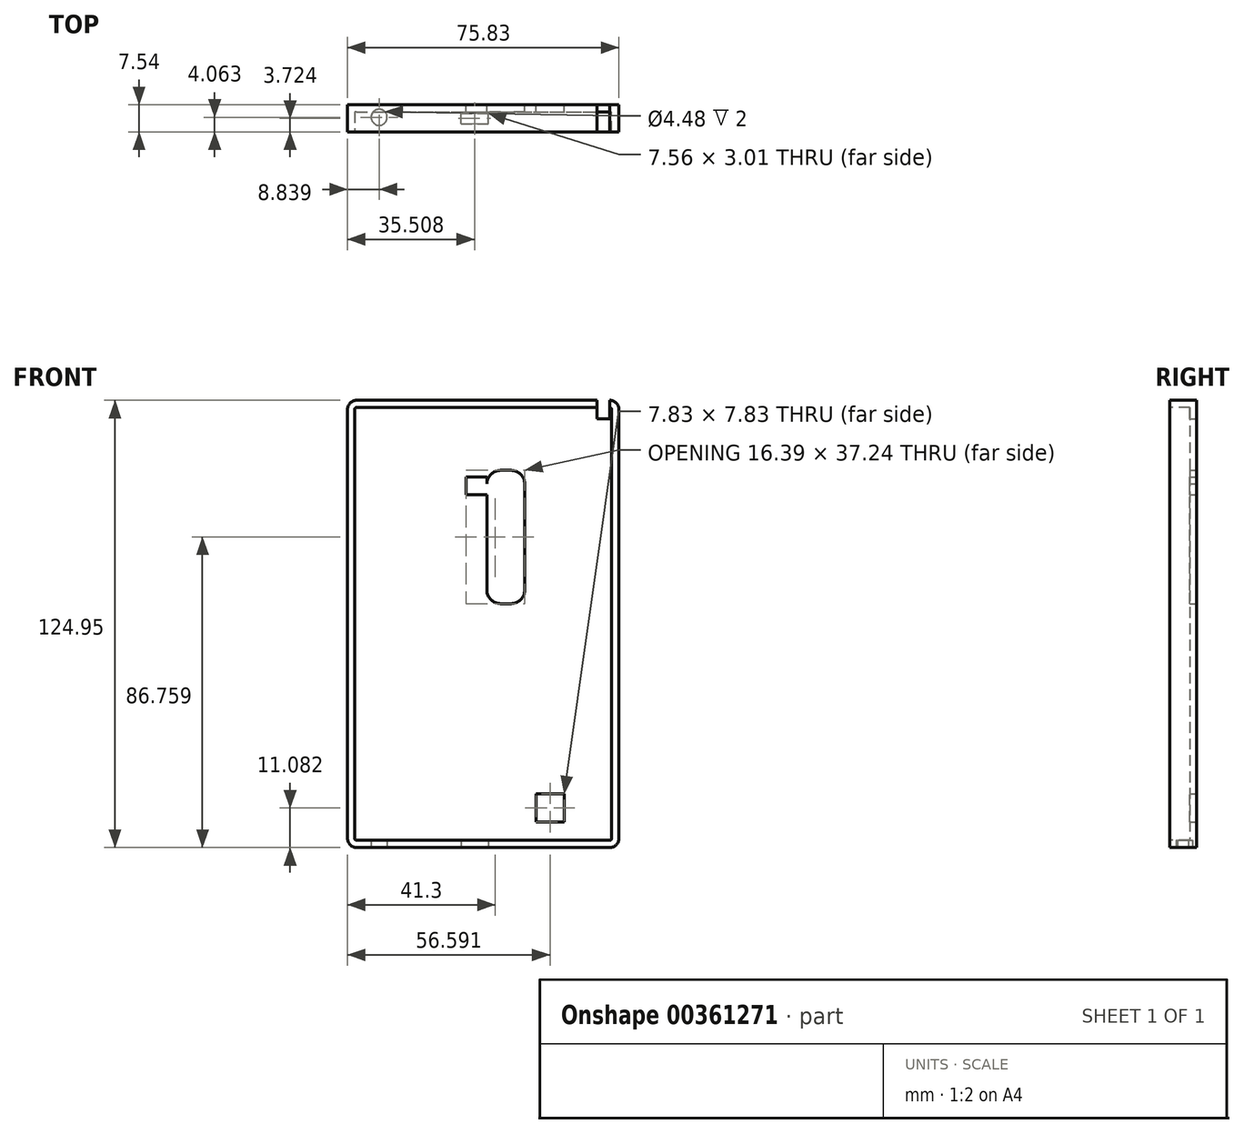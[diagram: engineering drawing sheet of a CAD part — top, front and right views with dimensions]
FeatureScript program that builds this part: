
annotation { "Feature Type Name" : "Feature", "Feature Type Description" : "" }
export const myFeature = defineFeature(function(context is Context, id is Id, definition is map)
    precondition{}
    {
        {
            var Q0;
            Q0=qCreatedBy(makeId("Front.planeOp"),FACE);
            var sketch = newSketch(context, id + "F0", { "sketchPlane" : qUnion([Q0])});
            skLineSegment(sketch, "E0.bottom", {"start": v(-33.05, 55.46) * mm, "end": v(37.7, 55.46) * mm});
            skLineSegment(sketch, "E0.top", {"start": v(-33.05, -69.49) * mm, "end": v(37.7, -69.49) * mm});
            skLineSegment(sketch, "E0.left", {"start": v(-35.6, 52.92) * mm, "end": v(-35.6, -66.95) * mm});
            skLineSegment(sketch, "E0.right", {"start": v(40.24, 52.92) * mm, "end": v(40.24, -66.95) * mm});
            skPoint(sketch, "E1.visualSharp", {"position": v(-35.6, 55.46) * mm});
            skArc(sketch, "E1.filletArc", {"start": v(-33.05, 55.46) * mm, "mid": v(-34.85, 54.72) * mm, "end": v(-35.6, 52.92) * mm});
            skPoint(sketch, "E2.visualSharp", {"position": v(40.24, 55.46) * mm});
            skArc(sketch, "E2.filletArc", {"start": v(40.24, 52.92) * mm, "mid": v(39.5, 54.72) * mm, "end": v(37.7, 55.46) * mm});
            skPoint(sketch, "E3.visualSharp", {"position": v(40.24, -69.49) * mm});
            skArc(sketch, "E3.filletArc", {"start": v(37.7, -69.49) * mm, "mid": v(39.5, -68.74) * mm, "end": v(40.24, -66.95) * mm});
            skPoint(sketch, "E4.visualSharp", {"position": v(-35.6, -69.49) * mm});
            skArc(sketch, "E4.filletArc", {"start": v(-35.6, -66.95) * mm, "mid": v(-34.85, -68.74) * mm, "end": v(-33.05, -69.49) * mm});
            skSolve(sketch);
        }
        {
            var Q0;
            Q0=makeQuery(id+"F0.imprint","IMPRINT",FACE,{"disambiguationData":[TD([[makeQuery(id+"F0.imprint","IMPRINT",EDGE,{"derivedFrom":sQuery(id+"F0.wireOp",EDGE,"E0.bottom")}),-1.0]])]});
            extrude(context, id + "F1", {"entities" : qUnion([Q0]), "oppositeDirection" : true, "depth" : 7.54 * mm});
        }
        {
            var Q0;
            Q0=makeQuery(id+"F1.opExtrude","SWEPT_FACE",FACE,{"disambiguationData":[OSD([sQuery(id+"F0.wireOp",EDGE,"E0.top")])]});
            var sketch = newSketch(context, id + "F2", { "sketchPlane" : qUnion([Q0])});
            skLineSegment(sketch, "E5.bottom", {"start": v(-3.86, -2.22) * mm, "end": v(3.7, -2.22) * mm});
            skLineSegment(sketch, "E5.top", {"start": v(-3.86, -5.23) * mm, "end": v(3.7, -5.23) * mm});
            skLineSegment(sketch, "E5.left", {"start": v(-3.86, -2.22) * mm, "end": v(-3.86, -5.23) * mm});
            skLineSegment(sketch, "E5.right", {"start": v(3.7, -2.22) * mm, "end": v(3.7, -5.23) * mm});
            skCircle(sketch, "E6", {"center": v(-26.75, -4.06) * mm, "radius": 2.24 * mm});
            skSolve(sketch);
        }
        {
            var Q0;
            Q0=makeQuery(id+"F1.opExtrude","CAP_FACE",FACE,{"disambiguationData":[OSD([sQuery(id+"F0.wireOp",EDGE,"E0.bottom"),sQuery(id+"F0.wireOp",EDGE,"E0.top"),sQuery(id+"F0.wireOp",EDGE,"E0.left"),sQuery(id+"F0.wireOp",EDGE,"E0.right"),sQuery(id+"F0.wireOp",EDGE,"E1.filletArc"),sQuery(id+"F0.wireOp",EDGE,"E2.filletArc"),sQuery(id+"F0.wireOp",EDGE,"E3.filletArc"),sQuery(id+"F0.wireOp",EDGE,"E4.filletArc")])],"isStart":false});
            var sketch = newSketch(context, id + "F3", { "sketchPlane" : qUnion([Q0])});
            skLineSegment(sketch, "E7.bottom", {"start": v(-10.1, 35.89) * mm, "end": v(-7.16, 35.89) * mm});
            skLineSegment(sketch, "E7.top", {"start": v(-10.1, -1.35) * mm, "end": v(-7.16, -1.35) * mm});
            skLineSegment(sketch, "E7.left", {"start": v(-13.9, 32.08) * mm, "end": v(-13.9, 2.46) * mm});
            skLineSegment(sketch, "E7.right", {"start": v(-3.35, 32.08) * mm, "end": v(-3.35, 2.46) * mm});
            skLineSegment(sketch, "E8.bottom", {"start": v(-13.9, 22.25) * mm, "end": v(-3.35, 22.25) * mm});
            skLineSegment(sketch, "E8.left", {"start": v(-13.9, 22.25) * mm, "end": v(-13.9, 2.46) * mm});
            skLineSegment(sketch, "E8.right", {"start": v(-3.35, 22.25) * mm, "end": v(-3.35, 2.46) * mm});
            skLineSegment(sketch, "E9.bottom", {"start": v(-12.5, 14.13) * mm, "end": v(-4.76, 14.13) * mm});
            skLineSegment(sketch, "E9.top", {"start": v(-12.5, 6.77) * mm, "end": v(-4.76, 6.77) * mm});
            skLineSegment(sketch, "E9.left", {"start": v(-12.5, 14.13) * mm, "end": v(-12.5, 6.77) * mm});
            skLineSegment(sketch, "E9.right", {"start": v(-4.76, 14.13) * mm, "end": v(-4.76, 6.77) * mm});
            skLineSegment(sketch, "E10.bottom", {"start": v(-3.35, 34.03) * mm, "end": v(2.49, 34.03) * mm});
            skLineSegment(sketch, "E10.top", {"start": v(-3.35, 29.07) * mm, "end": v(2.49, 29.07) * mm});
            skLineSegment(sketch, "E10.left", {"start": v(-3.35, 34.03) * mm, "end": v(-3.35, 29.07) * mm});
            skLineSegment(sketch, "E10.right", {"start": v(2.49, 34.03) * mm, "end": v(2.49, 29.07) * mm});
            skLineSegment(sketch, "E11.bottom", {"start": v(-37.7, 55.46) * mm, "end": v(-34.08, 55.46) * mm});
            skLineSegment(sketch, "E11.top", {"start": v(-37.7, 50.33) * mm, "end": v(-34.08, 50.33) * mm});
            skLineSegment(sketch, "E11.left", {"start": v(-37.7, 55.46) * mm, "end": v(-37.7, 50.33) * mm});
            skLineSegment(sketch, "E11.right", {"start": v(-34.08, 55.46) * mm, "end": v(-34.08, 50.33) * mm});
            skLineSegment(sketch, "E12.bottom", {"start": v(-24.92, -54.5) * mm, "end": v(-17.09, -54.5) * mm});
            skLineSegment(sketch, "E12.top", {"start": v(-24.92, -62.32) * mm, "end": v(-17.09, -62.32) * mm});
            skLineSegment(sketch, "E12.left", {"start": v(-24.92, -54.5) * mm, "end": v(-24.92, -62.32) * mm});
            skLineSegment(sketch, "E12.right", {"start": v(-17.09, -54.5) * mm, "end": v(-17.09, -62.32) * mm});
            skPoint(sketch, "E13.visualSharp", {"position": v(-13.9, 35.89) * mm});
            skArc(sketch, "E13.filletArc", {"start": v(-10.1, 35.89) * mm, "mid": v(-12.8, 34.77) * mm, "end": v(-13.9, 32.08) * mm});
            skPoint(sketch, "E14.visualSharp", {"position": v(-3.35, 35.89) * mm});
            skArc(sketch, "E14.filletArc", {"start": v(-3.35, 32.08) * mm, "mid": v(-4.47, 34.77) * mm, "end": v(-7.16, 35.89) * mm});
            skPoint(sketch, "E15.visualSharp", {"position": v(-13.9, -1.35) * mm});
            skArc(sketch, "E15.filletArc", {"start": v(-13.9, 2.46) * mm, "mid": v(-12.8, -0.24) * mm, "end": v(-10.1, -1.35) * mm});
            skPoint(sketch, "E16.visualSharp", {"position": v(-3.35, -1.35) * mm});
            skArc(sketch, "E16.filletArc", {"start": v(-7.16, -1.35) * mm, "mid": v(-4.47, -0.24) * mm, "end": v(-3.35, 2.46) * mm});
            skSolve(sketch);
        }
        {
            var Q0;
            Q0=makeQuery(id+"F1.opExtrude","CAP_FACE",FACE,{"disambiguationData":[OSD([sQuery(id+"F0.wireOp",EDGE,"E0.bottom"),sQuery(id+"F0.wireOp",EDGE,"E0.top"),sQuery(id+"F0.wireOp",EDGE,"E0.left"),sQuery(id+"F0.wireOp",EDGE,"E0.right"),sQuery(id+"F0.wireOp",EDGE,"E1.filletArc"),sQuery(id+"F0.wireOp",EDGE,"E2.filletArc"),sQuery(id+"F0.wireOp",EDGE,"E3.filletArc"),sQuery(id+"F0.wireOp",EDGE,"E4.filletArc")])],"isStart":true});
            shell(context, id + "F4", {"entities" : qUnion([Q0]), "thickness" : 2 * mm});
        }
        {
            var Q0;
            Q0 = qSketchRegion(id + "F3", true);
            extrude(context, id + "F5", {"entities" : qUnion([Q0]), "operationType" : NewBodyOperationType.REMOVE, "oppositeDirection" : true, "depth" : 50.8 * mm});
        }
        {
            var Q0;
            Q0=makeQuery(id+"F5.boolean.opBoolean","SPLIT",FACE,{"disambiguationData":[TD([makeQuery(id+"F5.opExtrude","SWEPT_FACE",FACE,{"disambiguationData":[OSD([sQuery(id+"F3.wireOp",EDGE,"E9.bottom")])]})])],"derivedFrom":makeQuery(id+"F1.opExtrude","CAP_FACE",FACE,{"disambiguationData":[OSD([sQuery(id+"F0.wireOp",EDGE,"E0.bottom"),sQuery(id+"F0.wireOp",EDGE,"E0.top"),sQuery(id+"F0.wireOp",EDGE,"E0.left"),sQuery(id+"F0.wireOp",EDGE,"E0.right"),sQuery(id+"F0.wireOp",EDGE,"E1.filletArc"),sQuery(id+"F0.wireOp",EDGE,"E2.filletArc"),sQuery(id+"F0.wireOp",EDGE,"E3.filletArc"),sQuery(id+"F0.wireOp",EDGE,"E4.filletArc")])],"isStart":false})});
            extrude(context, id + "F6", {"entities" : qUnion([Q0]), "operationType" : NewBodyOperationType.ADD, "depth" : 25.4 * mm});
        }
        {
            var Q0;
            Q0=makeQuery(id+"F6.opExtrude","CAP_FACE",FACE,{"disambiguationData":[OSD([sQuery(id+"F0.wireOp",EDGE,"E0.bottom"),sQuery(id+"F0.wireOp",EDGE,"E0.top"),sQuery(id+"F0.wireOp",EDGE,"E0.left"),sQuery(id+"F0.wireOp",EDGE,"E0.right"),sQuery(id+"F0.wireOp",EDGE,"E1.filletArc"),sQuery(id+"F0.wireOp",EDGE,"E2.filletArc"),sQuery(id+"F0.wireOp",EDGE,"E3.filletArc"),sQuery(id+"F0.wireOp",EDGE,"E4.filletArc")])],"isStart":false});
            extrude(context, id + "F7", {"entities" : qUnion([Q0]), "operationType" : NewBodyOperationType.REMOVE, "oppositeDirection" : true, "depth" : 50.8 * mm});
        }
        {
            var Q0;
            Q0=makeQuery(id+"F2.imprint","IMPRINT",FACE,{"disambiguationData":[TD([[makeQuery(id+"F2.imprint","IMPRINT",EDGE,{"derivedFrom":sQuery(id+"F2.wireOp",EDGE,"E6")}),1.0]])]});
            var Q1;
            Q1=makeQuery(id+"F2.imprint","IMPRINT",FACE,{"disambiguationData":[TD([[makeQuery(id+"F2.imprint","IMPRINT",EDGE,{"derivedFrom":sQuery(id+"F2.wireOp",EDGE,"E5.bottom")}),-1.0]])]});
            extrude(context, id + "F8", {"entities" : qUnion([Q0, Q1]), "operationType" : NewBodyOperationType.REMOVE, "oppositeDirection" : true, "depth" : 2 * mm});
        }
    });
